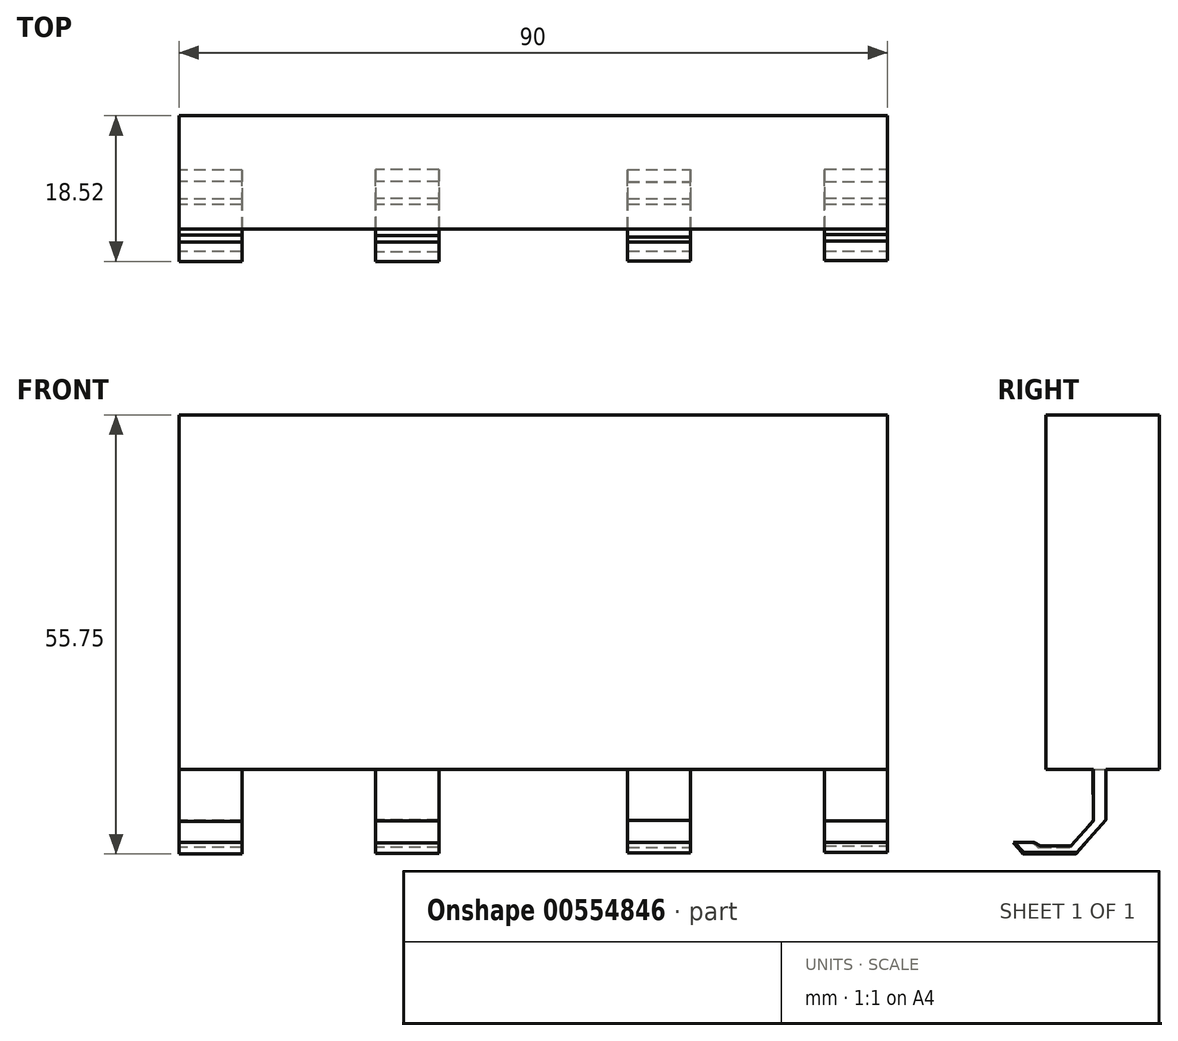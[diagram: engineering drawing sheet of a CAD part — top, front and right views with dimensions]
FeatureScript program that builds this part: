
annotation { "Feature Type Name" : "Feature", "Feature Type Description" : "" }
export const myFeature = defineFeature(function(context is Context, id is Id, definition is map)
    precondition{}
    {
        {
            var Q0;
            Q0=qCreatedBy(makeId("Front.planeOp"),FACE);
            var sketch = newSketch(context, id + "F0", { "sketchPlane" : qUnion([Q0])});
            skLineSegment(sketch, "E0.bottom", {"start": v(-62.63, 45) * mm, "end": v(27.37, 45) * mm});
            skLineSegment(sketch, "E0.top", {"start": v(-62.63, 0) * mm, "end": v(27.37, 0) * mm});
            skLineSegment(sketch, "E0.left", {"start": v(-62.63, 45) * mm, "end": v(-62.63, 0) * mm});
            skLineSegment(sketch, "E0.right", {"start": v(27.37, 45) * mm, "end": v(27.37, 0) * mm});
            skSolve(sketch);
        }
        {
            var Q0;
            Q0=makeQuery(id+"F0.imprint","IMPRINT",FACE,{"disambiguationData":[TD([[makeQuery(id+"F0.imprint","IMPRINT",EDGE,{"derivedFrom":sQuery(id+"F0.wireOp",EDGE,"E0.bottom")}),-1.0]])]});
            extrude(context, id + "F1", {"entities" : qUnion([Q0]), "depth" : 25 * mm, "offsetDistance" : 25 * mm});
        }
        {
            var Q0;
            Q0=makeQuery(id+"F1.opExtrude","SWEPT_FACE",FACE,{"disambiguationData":[OSD([sQuery(id+"F0.wireOp",EDGE,"E0.left")])]});
            var sketch = newSketch(context, id + "F2", { "sketchPlane" : qUnion([Q0])});
            skLineSegment(sketch, "E1", {"start": v(6.89, 0) * mm, "end": v(6.89, -6.5) * mm});
            skLineSegment(sketch, "E2", {"start": v(6.89, -6.5) * mm, "end": v(10.58, -10.75) * mm});
            skLineSegment(sketch, "E3", {"start": v(10.58, -10.75) * mm, "end": v(17.29, -10.75) * mm});
            skLineSegment(sketch, "E4", {"start": v(17.29, -10.75) * mm, "end": v(18.52, -9.31) * mm});
            skLineSegment(sketch, "E5", {"start": v(18.52, -9.31) * mm, "end": v(16.06, -9.31) * mm});
            skLineSegment(sketch, "E6", {"start": v(16.06, -9.31) * mm, "end": v(15.17, -9.93) * mm});
            skLineSegment(sketch, "E7", {"start": v(15.17, -9.93) * mm, "end": v(11.27, -9.93) * mm});
            skLineSegment(sketch, "E8", {"start": v(11.27, -9.93) * mm, "end": v(8.38, -6.61) * mm});
            skLineSegment(sketch, "E9", {"start": v(8.38, -6.61) * mm, "end": v(8.38, 0) * mm});
            skLineSegment(sketch, "E10", {"start": v(8.38, 0) * mm, "end": v(6.89, 0) * mm});
            skSolve(sketch);
        }
        {
            var Q0;
            Q0=makeQuery(id+"F2.imprint","IMPRINT",FACE,{"disambiguationData":[TD([[makeQuery(id+"F2.imprint","IMPRINT",EDGE,{"derivedFrom":sQuery(id+"F2.wireOp",EDGE,"E1")}),1.0]])]});
            extrude(context, id + "F3", {"entities" : qUnion([Q0]), "operationType" : NewBodyOperationType.ADD, "oppositeDirection" : true, "depth" : 8 * mm, "offsetDistance" : 25 * mm});
        }
        {
            var Q0;
            Q0=makeQuery(id+"F3.boolean.opBoolean","MERGE",FACE,{"derivedFrom":[makeQuery(id+"F1.opExtrude","SWEPT_FACE",FACE,{"disambiguationData":[OSD([sQuery(id+"F0.wireOp",EDGE,"E0.left")])]}),makeQuery(id+"F3.opExtrude","CAP_FACE",FACE,{"disambiguationData":[OSD([sQuery(id+"F2.wireOp",EDGE,"E1"),sQuery(id+"F2.wireOp",EDGE,"E2"),sQuery(id+"F2.wireOp",EDGE,"E3"),sQuery(id+"F2.wireOp",EDGE,"E4"),sQuery(id+"F2.wireOp",EDGE,"E5"),sQuery(id+"F2.wireOp",EDGE,"E6"),sQuery(id+"F2.wireOp",EDGE,"E7"),sQuery(id+"F2.wireOp",EDGE,"E8"),sQuery(id+"F2.wireOp",EDGE,"E9"),sQuery(id+"F2.wireOp",EDGE,"E10")])],"isStart":true})]});
            cPlane(context, id + "F4", {"entities" : qUnion([Q0]), "cplaneType" : CPlaneType.OFFSET, "offset" : 25 * mm, "oppositeDirection" : true, "width" : 150 * mm, "height" : 150 * mm});
        }
        {
            var Q0;
            Q0=qCreatedBy(id+"F4.planeOp",FACE);
            var sketch = newSketch(context, id + "F5", { "sketchPlane" : qUnion([Q0])});
            skLineSegment(sketch, "E11", {"start": v(6.82, 0) * mm, "end": v(6.82, -6.4) * mm});
            skLineSegment(sketch, "E12", {"start": v(6.82, -6.4) * mm, "end": v(10.51, -10.68) * mm});
            skLineSegment(sketch, "E13", {"start": v(10.51, -10.68) * mm, "end": v(17.32, -10.68) * mm});
            skLineSegment(sketch, "E14", {"start": v(17.32, -10.68) * mm, "end": v(18.52, -9.35) * mm});
            skLineSegment(sketch, "E15", {"start": v(18.52, -9.35) * mm, "end": v(16.05, -9.35) * mm});
            skLineSegment(sketch, "E16", {"start": v(16.05, -9.35) * mm, "end": v(15.23, -9.93) * mm});
            skLineSegment(sketch, "E17", {"start": v(15.23, -9.93) * mm, "end": v(11.27, -9.93) * mm});
            skLineSegment(sketch, "E18", {"start": v(11.27, -9.93) * mm, "end": v(8.36, -6.55) * mm});
            skLineSegment(sketch, "E19", {"start": v(8.36, -6.55) * mm, "end": v(8.36, 0) * mm});
            skLineSegment(sketch, "E20", {"start": v(8.36, 0) * mm, "end": v(6.82, 0) * mm});
            skSolve(sketch);
        }
        {
            var Q0;
            Q0=makeQuery(id+"F5.imprint","IMPRINT",FACE,{"disambiguationData":[TD([[makeQuery(id+"F5.imprint","IMPRINT",EDGE,{"derivedFrom":sQuery(id+"F5.wireOp",EDGE,"E11")}),1.0]])]});
            extrude(context, id + "F6", {"entities" : qUnion([Q0]), "operationType" : NewBodyOperationType.ADD, "oppositeDirection" : true, "depth" : 8 * mm, "offsetDistance" : 25 * mm});
        }
        {
            var Q0;
            Q0=makeQuery(id+"F1.opExtrude","SWEPT_FACE",FACE,{"disambiguationData":[OSD([sQuery(id+"F0.wireOp",EDGE,"E0.right")])]});
            var sketch = newSketch(context, id + "F7", { "sketchPlane" : qUnion([Q0])});
            skLineSegment(sketch, "E21", {"start": v(-8.38, 0) * mm, "end": v(-6.8, 0) * mm});
            skLineSegment(sketch, "E22", {"start": v(-6.8, 0) * mm, "end": v(-6.8, -6.44) * mm});
            skLineSegment(sketch, "E23", {"start": v(-6.8, -6.44) * mm, "end": v(-10.46, -10.59) * mm});
            skLineSegment(sketch, "E24", {"start": v(-10.46, -10.59) * mm, "end": v(-17.2, -10.59) * mm});
            skLineSegment(sketch, "E25", {"start": v(-17.2, -10.59) * mm, "end": v(-18.39, -9.29) * mm});
            skLineSegment(sketch, "E26", {"start": v(-18.39, -9.29) * mm, "end": v(-15.95, -9.29) * mm});
            skLineSegment(sketch, "E27", {"start": v(-15.95, -9.29) * mm, "end": v(-15.1, -9.73) * mm});
            skLineSegment(sketch, "E28", {"start": v(-15.1, -9.73) * mm, "end": v(-11.23, -9.73) * mm});
            skLineSegment(sketch, "E29", {"start": v(-11.23, -9.73) * mm, "end": v(-8.34, -6.56) * mm});
            skLineSegment(sketch, "E30", {"start": v(-8.34, -6.56) * mm, "end": v(-8.38, 0) * mm});
            skSolve(sketch);
        }
        {
            var Q0;
            Q0=makeQuery(id+"F7.imprint","IMPRINT",FACE,{"disambiguationData":[TD([[makeQuery(id+"F7.imprint","IMPRINT",EDGE,{"derivedFrom":sQuery(id+"F7.wireOp",EDGE,"E21")}),-1.0]])]});
            extrude(context, id + "F8", {"entities" : qUnion([Q0]), "operationType" : NewBodyOperationType.ADD, "oppositeDirection" : true, "depth" : 8 * mm, "offsetDistance" : 25 * mm});
        }
        {
            var Q0;
            Q0=makeQuery(id+"F8.boolean.opBoolean","MERGE",FACE,{"derivedFrom":[makeQuery(id+"F1.opExtrude","SWEPT_FACE",FACE,{"disambiguationData":[OSD([sQuery(id+"F0.wireOp",EDGE,"E0.right")])]}),makeQuery(id+"F8.opExtrude","CAP_FACE",FACE,{"disambiguationData":[OSD([sQuery(id+"F7.wireOp",EDGE,"E21"),sQuery(id+"F7.wireOp",EDGE,"E22"),sQuery(id+"F7.wireOp",EDGE,"E23"),sQuery(id+"F7.wireOp",EDGE,"E24"),sQuery(id+"F7.wireOp",EDGE,"E25"),sQuery(id+"F7.wireOp",EDGE,"E26"),sQuery(id+"F7.wireOp",EDGE,"E27"),sQuery(id+"F7.wireOp",EDGE,"E28"),sQuery(id+"F7.wireOp",EDGE,"E29"),sQuery(id+"F7.wireOp",EDGE,"E30")])],"isStart":true})]});
            cPlane(context, id + "F9", {"entities" : qUnion([Q0]), "cplaneType" : CPlaneType.OFFSET, "offset" : 25 * mm, "oppositeDirection" : true, "width" : 150 * mm, "height" : 150 * mm});
        }
        {
            var Q0;
            Q0=qCreatedBy(id+"F9.planeOp",FACE);
            var sketch = newSketch(context, id + "F10", { "sketchPlane" : qUnion([Q0])});
            skLineSegment(sketch, "E31", {"start": v(-8.43, 0) * mm, "end": v(-6.82, 0) * mm});
            skLineSegment(sketch, "E32", {"start": v(-6.82, 0) * mm, "end": v(-6.82, -6.47) * mm});
            skLineSegment(sketch, "E33", {"start": v(-6.82, -6.47) * mm, "end": v(-10.56, -10.64) * mm});
            skLineSegment(sketch, "E34", {"start": v(-10.56, -10.64) * mm, "end": v(-17.17, -10.64) * mm});
            skLineSegment(sketch, "E35", {"start": v(-17.17, -10.64) * mm, "end": v(-18.5, -9.28) * mm});
            skLineSegment(sketch, "E36", {"start": v(-18.5, -9.28) * mm, "end": v(-16.08, -9.28) * mm});
            skLineSegment(sketch, "E37", {"start": v(-16.08, -9.28) * mm, "end": v(-15.4, -9.95) * mm});
            skLineSegment(sketch, "E38", {"start": v(-15.4, -9.95) * mm, "end": v(-11.25, -9.95) * mm});
            skLineSegment(sketch, "E39", {"start": v(-11.25, -9.95) * mm, "end": v(-8.34, -6.5) * mm});
            skLineSegment(sketch, "E40", {"start": v(-8.34, -6.5) * mm, "end": v(-8.43, 0) * mm});
            skSolve(sketch);
        }
        {
            var Q0;
            Q0 = qSketchRegion(id + "F10", true);
            extrude(context, id + "F11", {"entities" : qUnion([Q0]), "operationType" : NewBodyOperationType.ADD, "oppositeDirection" : true, "depth" : 8 * mm, "offsetDistance" : 25 * mm});
        }
        {
            var Q0;
            Q0=makeQuery(id+"F8.boolean.opBoolean","MERGE",FACE,{"derivedFrom":[makeQuery(id+"F1.opExtrude","SWEPT_FACE",FACE,{"disambiguationData":[OSD([sQuery(id+"F0.wireOp",EDGE,"E0.right")])]}),makeQuery(id+"F8.opExtrude","CAP_FACE",FACE,{"disambiguationData":[OSD([sQuery(id+"F7.wireOp",EDGE,"E21"),sQuery(id+"F7.wireOp",EDGE,"E22"),sQuery(id+"F7.wireOp",EDGE,"E23"),sQuery(id+"F7.wireOp",EDGE,"E24"),sQuery(id+"F7.wireOp",EDGE,"E25"),sQuery(id+"F7.wireOp",EDGE,"E26"),sQuery(id+"F7.wireOp",EDGE,"E27"),sQuery(id+"F7.wireOp",EDGE,"E28"),sQuery(id+"F7.wireOp",EDGE,"E29"),sQuery(id+"F7.wireOp",EDGE,"E30")])],"isStart":true})]});
            var sketch = newSketch(context, id + "F12", { "sketchPlane" : qUnion([Q0])});
            skLineSegment(sketch, "E41", {"start": v(-14.38, 0) * mm, "end": v(-14.38, 45.95) * mm});
            skLineSegment(sketch, "E42", {"start": v(-14.38, 45.95) * mm, "end": v(-25.9, 45.95) * mm});
            skLineSegment(sketch, "E43", {"start": v(-25.9, 45.95) * mm, "end": v(-25.9, -0.97) * mm});
            skLineSegment(sketch, "E44", {"start": v(-25.9, -0.97) * mm, "end": v(-14.38, -0.97) * mm});
            skLineSegment(sketch, "E45", {"start": v(-14.38, -0.97) * mm, "end": v(-14.38, 0) * mm});
            skSolve(sketch);
        }
        {
            var Q0;
            Q0 = qSketchRegion(id + "F12", true);
            extrude(context, id + "F13", {"entities" : qUnion([Q0]), "operationType" : NewBodyOperationType.REMOVE, "oppositeDirection" : true, "depth" : 100 * mm, "offsetDistance" : 25 * mm});
        }
    });
